# Revit family: FU_Chair_Sandler_Woodlook 2-6C
name_source: partatom
category: Furniture
units: mm (PartAtom-declared; Revit-internal decimal feet)

## family parameters
Always vertical = Yes
Cut with Voids When Loaded = No
OmniClass Number = 23.40.20.00
OmniClass Title = General Furniture and Specialties
Room Calculation Point = No
Shared = No
Work Plane-Based = No

## types (1)
- Woodlook 2.6C
    Default Elevation = 0 mm  [stored 0 ft]
    Depth = 655 mm  [stored 2.14895 ft]
    Description = Woodlook armchair with frame manufactured entirely from aluminum but with realistic appearance of wood. With casters in nylon (suitable for carpet floors) or polyurethane (suitable for wood or tile floors). Highly durable and scratch resistant.
    Height = 1015 mm  [stored 3.33005 ft]
    Manufacturer = Sandler
    Model = Woodlook 2.6C
    URL = https://www.sandlerseating.com
    Upholstery = Woodlook Vinyl - Dream
    Width = 590 mm  [stored 1.9357 ft]
    Woodlook = Woodlook - 25 Wenge

note: [stored X ft] marks values corroborated as IEEE doubles in the binary element streams (Revit-internal decimal feet)

## geometry (parser evidence)
native form markers: Sweep x5
no freeform markers — native parametric forms only
